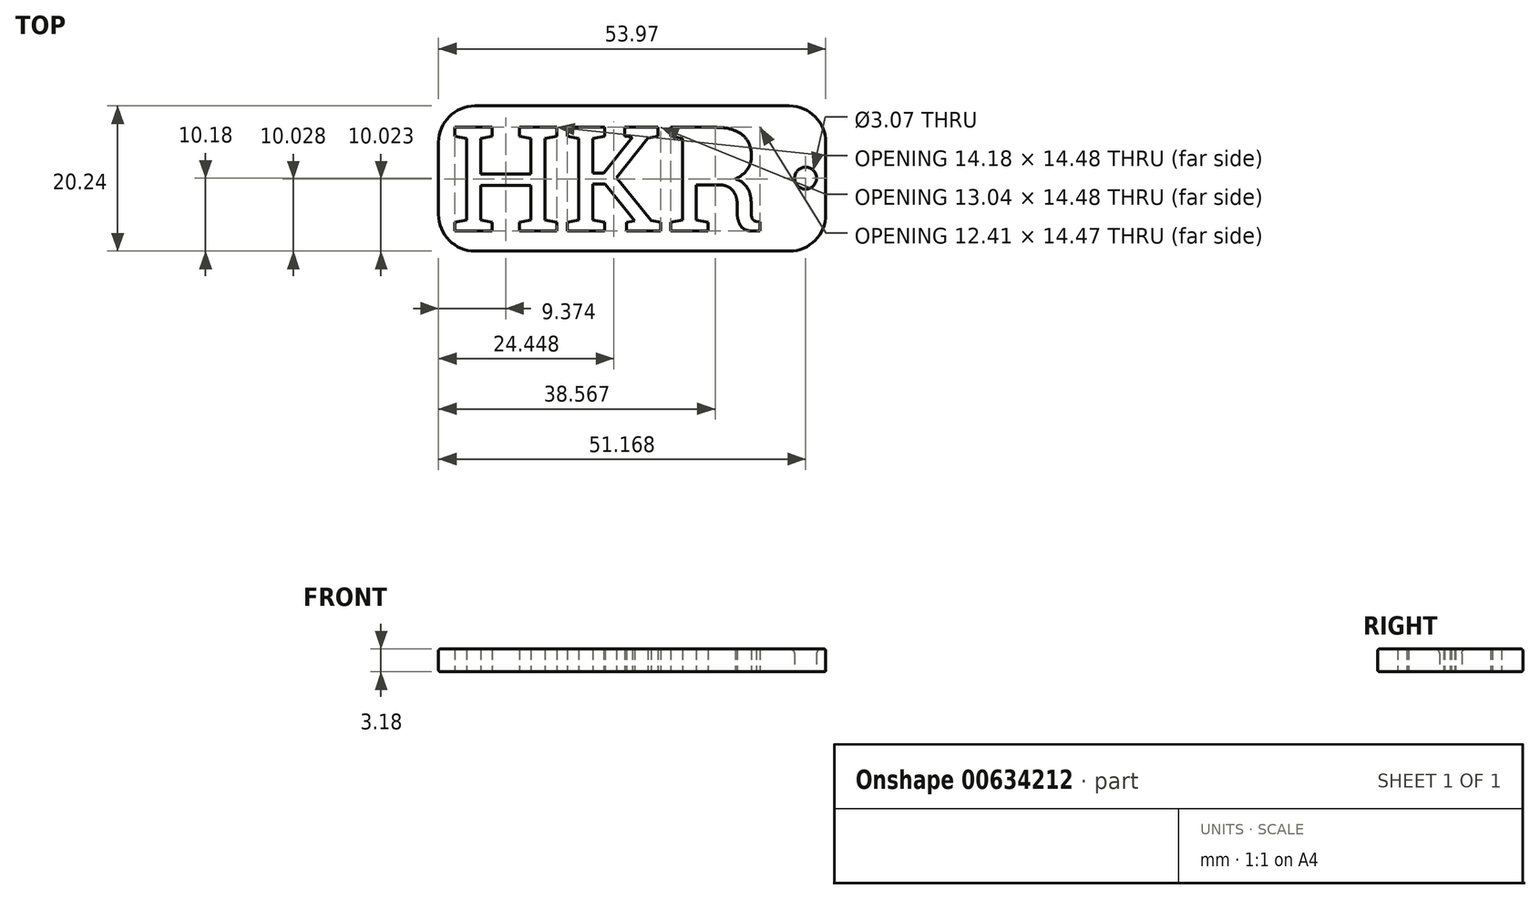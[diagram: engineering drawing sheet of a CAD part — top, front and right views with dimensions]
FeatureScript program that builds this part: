
annotation { "Feature Type Name" : "Feature", "Feature Type Description" : "" }
export const myFeature = defineFeature(function(context is Context, id is Id, definition is map)
    precondition{}
    {
        {
            var Q0;
            Q0=qCreatedBy(makeId("Top.planeOp"),FACE);
            var sketch = newSketch(context, id + "F0", { "sketchPlane" : qUnion([Q0])});
            skLineSegment(sketch, "E0.bottom", {"start": v(-77.06, 7.36) * mm, "end": v(-23.09, 7.36) * mm});
            skLineSegment(sketch, "E0.top", {"start": v(-77.06, -12.88) * mm, "end": v(-23.09, -12.88) * mm});
            skLineSegment(sketch, "E0.left", {"start": v(-77.06, 7.36) * mm, "end": v(-77.06, -12.88) * mm});
            skLineSegment(sketch, "E0.right", {"start": v(-23.09, 7.36) * mm, "end": v(-23.09, -12.88) * mm});
            skSolve(sketch);
        }
        {
            var Q0;
            Q0=makeQuery(id+"F0.imprint","IMPRINT",FACE,{"disambiguationData":[TD([[makeQuery(id+"F0.imprint","IMPRINT",EDGE,{"derivedFrom":sQuery(id+"F0.wireOp",EDGE,"E0.bottom")}),-1.0]])]});
            var sketch = newSketch(context, id + "F1", { "sketchPlane" : qUnion([Q0])});
            skText(sketch, "E1", { "text": "HKR", "fontName": "RobotoSlab-Regular.ttf"});
            const initialGuessF1  = {"E1": [-0.07548, -0.01009, 1, 0, 0.01466]};
            skSetInitialGuess(sketch, initialGuessF1);
            skSolve(sketch);
        }
        {
            var Q0;
            Q0=makeQuery(id+"F0.imprint","IMPRINT",FACE,{"disambiguationData":[TD([[makeQuery(id+"F0.imprint","IMPRINT",EDGE,{"derivedFrom":sQuery(id+"F0.wireOp",EDGE,"E0.bottom")}),-1.0]])]});
            var sketch = newSketch(context, id + "F2", { "sketchPlane" : qUnion([Q0])});
            skCircle(sketch, "E2", {"center": v(-25.9, -2.7) * mm, "radius": 1.53 * mm});
            skSolve(sketch);
        }
        {
            var Q0;
            Q0=makeQuery(id+"F0.imprint","IMPRINT",FACE,{"disambiguationData":[TD([[makeQuery(id+"F0.imprint","IMPRINT",EDGE,{"derivedFrom":sQuery(id+"F0.wireOp",EDGE,"E0.bottom")}),-1.0]])]});
            extrude(context, id + "F3", {"entities" : qUnion([Q0]), "depth" : 3.17 * mm, "offsetDistance" : 25.4 * mm});
        }
        {
            var Q0;
            Q0 = qSketchRegion(id + "F2", true);
            extrude(context, id + "F4", {"entities" : qUnion([Q0]), "operationType" : NewBodyOperationType.REMOVE, "depth" : 25.4 * mm, "offsetDistance" : 25.4 * mm});
        }
        {
            var Q0;
            Q0 = qSketchRegion(id + "F1", true);
            extrude(context, id + "F5", {"entities" : qUnion([Q0]), "operationType" : NewBodyOperationType.REMOVE, "depth" : 25.4 * mm, "offsetDistance" : 25.4 * mm});
        }
        {
            var Q0;
            Q0=makeQuery(id+"F3.opExtrude","SWEPT_EDGE",EDGE,{"disambiguationData":[OSD([sQuery(id+"F0.wireOp",EDGE,"E0.bottom"),sQuery(id+"F0.wireOp",EDGE,"E0.right")])]});
            fillet(context, id + "F6", {"entities" : qUnion([Q0]), "radius" : 5.08 * mm, "tangentPropagation" : true, "allowEdgeOverflow" : false});
        }
        {
            var Q0;
            Q0=makeQuery(id+"F3.opExtrude","SWEPT_EDGE",EDGE,{"disambiguationData":[OSD([sQuery(id+"F0.wireOp",EDGE,"E0.top"),sQuery(id+"F0.wireOp",EDGE,"E0.right")])]});
            fillet(context, id + "F7", {"entities" : qUnion([Q0]), "radius" : 5.08 * mm, "tangentPropagation" : true, "allowEdgeOverflow" : false});
        }
        {
            var Q0;
            Q0=makeQuery(id+"F3.opExtrude","SWEPT_EDGE",EDGE,{"disambiguationData":[OSD([sQuery(id+"F0.wireOp",EDGE,"E0.top"),sQuery(id+"F0.wireOp",EDGE,"E0.left")])]});
            fillet(context, id + "F8", {"entities" : qUnion([Q0]), "radius" : 5.08 * mm, "tangentPropagation" : true, "allowEdgeOverflow" : false});
        }
        {
            var Q0;
            Q0=makeQuery(id+"F3.opExtrude","SWEPT_EDGE",EDGE,{"disambiguationData":[OSD([sQuery(id+"F0.wireOp",EDGE,"E0.bottom"),sQuery(id+"F0.wireOp",EDGE,"E0.left")])]});
            fillet(context, id + "F9", {"entities" : qUnion([Q0]), "radius" : 5.08 * mm, "tangentPropagation" : true, "allowEdgeOverflow" : false});
        }
        {
            var Q0;
            Q0=makeQuery(id+"F4.boolean.opBoolean","INTERSECT",EDGE,{"derivedFrom":[makeQuery(id+"F3.opExtrude","CAP_FACE",FACE,{"disambiguationData":[OSD([sQuery(id+"F0.wireOp",EDGE,"E0.bottom"),sQuery(id+"F0.wireOp",EDGE,"E0.top"),sQuery(id+"F0.wireOp",EDGE,"E0.left"),sQuery(id+"F0.wireOp",EDGE,"E0.right")])],"isStart":false}),makeQuery(id+"F4.opExtrude","SWEPT_FACE",FACE,{"disambiguationData":[OSD([sQuery(id+"F2.wireOp",EDGE,"E2")])]})]});
            var Q1;
            Q1=makeQuery(id+"F4.boolean.opBoolean","COPY",EDGE,{"derivedFrom":makeQuery(id+"F4.opExtrude","CAP_EDGE",EDGE,{"disambiguationData":[OSD([sQuery(id+"F2.wireOp",EDGE,"E2")])],"isStart":true})});
            fillet(context, id + "F10", {"entities" : qUnion([Q0, Q1]), "radius" : 0.64 * mm, "tangentPropagation" : true, "allowEdgeOverflow" : false});
        }
        {
            var Q0;
            Q0=makeQuery(id+"F3.opExtrude","CAP_EDGE",EDGE,{"disambiguationData":[OSD([sQuery(id+"F0.wireOp",EDGE,"E0.bottom")])],"isStart":false});
            var Q1;
            {var subQ0=sQuery(id+"F0.wireOp",EDGE,"E0.left");var subQ1=sQuery(id+"F0.wireOp",EDGE,"E0.bottom");var subQ2=sQuery(id+"F0.wireOp",EDGE,"E0.right");var subQ3=sQuery(id+"F0.wireOp",EDGE,"E0.top");Q1=makeQuery(id+"F9.opFillet","BLEND_EDGE",EDGE,{"blendedFrom":[makeQuery(id+"F3.opExtrude","SWEPT_EDGE",EDGE,{"disambiguationData":[OSD([subQ1,subQ0])]}),makeQuery(id+"F5.boolean.opBoolean","SPLIT",FACE,{"disambiguationData":[TD([makeQuery(id+"F3.opExtrude","SWEPT_FACE",FACE,{"disambiguationData":[OSD([subQ1])]})])],"derivedFrom":makeQuery(id+"F3.opExtrude","CAP_FACE",FACE,{"disambiguationData":[OSD([subQ1,subQ3,subQ0,subQ2])],"isStart":false})})],"blendedInto":[makeQuery(id+"F5.boolean.opBoolean","SPLIT",FACE,{"disambiguationData":[TD([makeQuery(id+"F3.opExtrude","SWEPT_FACE",FACE,{"disambiguationData":[OSD([subQ1])]})])],"derivedFrom":makeQuery(id+"F3.opExtrude","CAP_FACE",FACE,{"disambiguationData":[OSD([subQ1,subQ3,subQ0,subQ2])],"isStart":false})})]});}
            var Q2;
            Q2=makeQuery(id+"F3.opExtrude","CAP_EDGE",EDGE,{"disambiguationData":[OSD([sQuery(id+"F0.wireOp",EDGE,"E0.left")])],"isStart":false});
            var Q3;
            {var subQ0=sQuery(id+"F0.wireOp",EDGE,"E0.left");var subQ1=sQuery(id+"F0.wireOp",EDGE,"E0.bottom");var subQ2=sQuery(id+"F0.wireOp",EDGE,"E0.right");var subQ3=sQuery(id+"F0.wireOp",EDGE,"E0.top");Q3=makeQuery(id+"F8.opFillet","BLEND_EDGE",EDGE,{"blendedFrom":[makeQuery(id+"F3.opExtrude","SWEPT_EDGE",EDGE,{"disambiguationData":[OSD([subQ3,subQ0])]}),makeQuery(id+"F5.boolean.opBoolean","SPLIT",FACE,{"disambiguationData":[TD([makeQuery(id+"F3.opExtrude","SWEPT_FACE",FACE,{"disambiguationData":[OSD([subQ1])]})])],"derivedFrom":makeQuery(id+"F3.opExtrude","CAP_FACE",FACE,{"disambiguationData":[OSD([subQ1,subQ3,subQ0,subQ2])],"isStart":false})})],"blendedInto":[makeQuery(id+"F5.boolean.opBoolean","SPLIT",FACE,{"disambiguationData":[TD([makeQuery(id+"F3.opExtrude","SWEPT_FACE",FACE,{"disambiguationData":[OSD([subQ1])]})])],"derivedFrom":makeQuery(id+"F3.opExtrude","CAP_FACE",FACE,{"disambiguationData":[OSD([subQ1,subQ3,subQ0,subQ2])],"isStart":false})})]});}
            var Q4;
            Q4=makeQuery(id+"F3.opExtrude","CAP_EDGE",EDGE,{"disambiguationData":[OSD([sQuery(id+"F0.wireOp",EDGE,"E0.top")])],"isStart":false});
            var Q5;
            {var subQ0=sQuery(id+"F0.wireOp",EDGE,"E0.left");var subQ1=sQuery(id+"F0.wireOp",EDGE,"E0.bottom");var subQ2=sQuery(id+"F0.wireOp",EDGE,"E0.right");var subQ3=sQuery(id+"F0.wireOp",EDGE,"E0.top");Q5=makeQuery(id+"F6.opFillet","BLEND_EDGE",EDGE,{"blendedFrom":[makeQuery(id+"F3.opExtrude","SWEPT_EDGE",EDGE,{"disambiguationData":[OSD([subQ1,subQ2])]}),makeQuery(id+"F5.boolean.opBoolean","SPLIT",FACE,{"disambiguationData":[TD([makeQuery(id+"F3.opExtrude","SWEPT_FACE",FACE,{"disambiguationData":[OSD([subQ1])]})])],"derivedFrom":makeQuery(id+"F3.opExtrude","CAP_FACE",FACE,{"disambiguationData":[OSD([subQ1,subQ3,subQ0,subQ2])],"isStart":false})})],"blendedInto":[makeQuery(id+"F5.boolean.opBoolean","SPLIT",FACE,{"disambiguationData":[TD([makeQuery(id+"F3.opExtrude","SWEPT_FACE",FACE,{"disambiguationData":[OSD([subQ1])]})])],"derivedFrom":makeQuery(id+"F3.opExtrude","CAP_FACE",FACE,{"disambiguationData":[OSD([subQ1,subQ3,subQ0,subQ2])],"isStart":false})})]});}
            var Q6;
            Q6=makeQuery(id+"F3.opExtrude","CAP_EDGE",EDGE,{"disambiguationData":[OSD([sQuery(id+"F0.wireOp",EDGE,"E0.right")])],"isStart":true});
            var Q7;
            {var subQ0=sQuery(id+"F0.wireOp",EDGE,"E0.left");var subQ1=sQuery(id+"F0.wireOp",EDGE,"E0.bottom");var subQ2=sQuery(id+"F0.wireOp",EDGE,"E0.right");var subQ3=sQuery(id+"F0.wireOp",EDGE,"E0.top");Q7=makeQuery(id+"F7.opFillet","BLEND_EDGE",EDGE,{"blendedFrom":[makeQuery(id+"F3.opExtrude","SWEPT_EDGE",EDGE,{"disambiguationData":[OSD([subQ3,subQ2])]}),makeQuery(id+"F5.boolean.opBoolean","SPLIT",FACE,{"disambiguationData":[TD([makeQuery(id+"F3.opExtrude","SWEPT_FACE",FACE,{"disambiguationData":[OSD([subQ1])]})])],"derivedFrom":makeQuery(id+"F3.opExtrude","CAP_FACE",FACE,{"disambiguationData":[OSD([subQ1,subQ3,subQ0,subQ2])],"isStart":false})})],"blendedInto":[makeQuery(id+"F5.boolean.opBoolean","SPLIT",FACE,{"disambiguationData":[TD([makeQuery(id+"F3.opExtrude","SWEPT_FACE",FACE,{"disambiguationData":[OSD([subQ1])]})])],"derivedFrom":makeQuery(id+"F3.opExtrude","CAP_FACE",FACE,{"disambiguationData":[OSD([subQ1,subQ3,subQ0,subQ2])],"isStart":false})})]});}
            var Q8;
            Q8=makeQuery(id+"F3.opExtrude","CAP_EDGE",EDGE,{"disambiguationData":[OSD([sQuery(id+"F0.wireOp",EDGE,"E0.right")])],"isStart":false});
            var Q9;
            {var subQ0=sQuery(id+"F0.wireOp",EDGE,"E0.left");var subQ1=sQuery(id+"F0.wireOp",EDGE,"E0.bottom");var subQ2=sQuery(id+"F0.wireOp",EDGE,"E0.right");var subQ3=sQuery(id+"F0.wireOp",EDGE,"E0.top");Q9=makeQuery(id+"F6.opFillet","BLEND_EDGE",EDGE,{"blendedFrom":[makeQuery(id+"F3.opExtrude","SWEPT_EDGE",EDGE,{"disambiguationData":[OSD([subQ1,subQ2])]}),makeQuery(id+"F5.boolean.opBoolean","SPLIT",FACE,{"disambiguationData":[TD([makeQuery(id+"F3.opExtrude","SWEPT_FACE",FACE,{"disambiguationData":[OSD([subQ1])]})])],"derivedFrom":makeQuery(id+"F3.opExtrude","CAP_FACE",FACE,{"disambiguationData":[OSD([subQ1,subQ3,subQ0,subQ2])],"isStart":true})})],"blendedInto":[makeQuery(id+"F5.boolean.opBoolean","SPLIT",FACE,{"disambiguationData":[TD([makeQuery(id+"F3.opExtrude","SWEPT_FACE",FACE,{"disambiguationData":[OSD([subQ1])]})])],"derivedFrom":makeQuery(id+"F3.opExtrude","CAP_FACE",FACE,{"disambiguationData":[OSD([subQ1,subQ3,subQ0,subQ2])],"isStart":true})})]});}
            var Q10;
            Q10=makeQuery(id+"F3.opExtrude","CAP_EDGE",EDGE,{"disambiguationData":[OSD([sQuery(id+"F0.wireOp",EDGE,"E0.bottom")])],"isStart":true});
            var Q11;
            {var subQ0=sQuery(id+"F0.wireOp",EDGE,"E0.left");var subQ1=sQuery(id+"F0.wireOp",EDGE,"E0.bottom");var subQ2=sQuery(id+"F0.wireOp",EDGE,"E0.right");var subQ3=sQuery(id+"F0.wireOp",EDGE,"E0.top");Q11=makeQuery(id+"F7.opFillet","BLEND_EDGE",EDGE,{"blendedFrom":[makeQuery(id+"F3.opExtrude","SWEPT_EDGE",EDGE,{"disambiguationData":[OSD([subQ3,subQ2])]}),makeQuery(id+"F5.boolean.opBoolean","SPLIT",FACE,{"disambiguationData":[TD([makeQuery(id+"F3.opExtrude","SWEPT_FACE",FACE,{"disambiguationData":[OSD([subQ1])]})])],"derivedFrom":makeQuery(id+"F3.opExtrude","CAP_FACE",FACE,{"disambiguationData":[OSD([subQ1,subQ3,subQ0,subQ2])],"isStart":true})})],"blendedInto":[makeQuery(id+"F5.boolean.opBoolean","SPLIT",FACE,{"disambiguationData":[TD([makeQuery(id+"F3.opExtrude","SWEPT_FACE",FACE,{"disambiguationData":[OSD([subQ1])]})])],"derivedFrom":makeQuery(id+"F3.opExtrude","CAP_FACE",FACE,{"disambiguationData":[OSD([subQ1,subQ3,subQ0,subQ2])],"isStart":true})})]});}
            var Q12;
            {var subQ0=sQuery(id+"F0.wireOp",EDGE,"E0.left");var subQ1=sQuery(id+"F0.wireOp",EDGE,"E0.bottom");var subQ2=sQuery(id+"F0.wireOp",EDGE,"E0.right");var subQ3=sQuery(id+"F0.wireOp",EDGE,"E0.top");Q12=makeQuery(id+"F9.opFillet","BLEND_EDGE",EDGE,{"blendedFrom":[makeQuery(id+"F3.opExtrude","SWEPT_EDGE",EDGE,{"disambiguationData":[OSD([subQ1,subQ0])]}),makeQuery(id+"F5.boolean.opBoolean","SPLIT",FACE,{"disambiguationData":[TD([makeQuery(id+"F3.opExtrude","SWEPT_FACE",FACE,{"disambiguationData":[OSD([subQ1])]})])],"derivedFrom":makeQuery(id+"F3.opExtrude","CAP_FACE",FACE,{"disambiguationData":[OSD([subQ1,subQ3,subQ0,subQ2])],"isStart":true})})],"blendedInto":[makeQuery(id+"F5.boolean.opBoolean","SPLIT",FACE,{"disambiguationData":[TD([makeQuery(id+"F3.opExtrude","SWEPT_FACE",FACE,{"disambiguationData":[OSD([subQ1])]})])],"derivedFrom":makeQuery(id+"F3.opExtrude","CAP_FACE",FACE,{"disambiguationData":[OSD([subQ1,subQ3,subQ0,subQ2])],"isStart":true})})]});}
            var Q13;
            Q13=makeQuery(id+"F3.opExtrude","CAP_EDGE",EDGE,{"disambiguationData":[OSD([sQuery(id+"F0.wireOp",EDGE,"E0.left")])],"isStart":true});
            var Q14;
            {var subQ0=sQuery(id+"F0.wireOp",EDGE,"E0.left");var subQ1=sQuery(id+"F0.wireOp",EDGE,"E0.bottom");var subQ2=sQuery(id+"F0.wireOp",EDGE,"E0.right");var subQ3=sQuery(id+"F0.wireOp",EDGE,"E0.top");Q14=makeQuery(id+"F8.opFillet","BLEND_EDGE",EDGE,{"blendedFrom":[makeQuery(id+"F3.opExtrude","SWEPT_EDGE",EDGE,{"disambiguationData":[OSD([subQ3,subQ0])]}),makeQuery(id+"F5.boolean.opBoolean","SPLIT",FACE,{"disambiguationData":[TD([makeQuery(id+"F3.opExtrude","SWEPT_FACE",FACE,{"disambiguationData":[OSD([subQ1])]})])],"derivedFrom":makeQuery(id+"F3.opExtrude","CAP_FACE",FACE,{"disambiguationData":[OSD([subQ1,subQ3,subQ0,subQ2])],"isStart":true})})],"blendedInto":[makeQuery(id+"F5.boolean.opBoolean","SPLIT",FACE,{"disambiguationData":[TD([makeQuery(id+"F3.opExtrude","SWEPT_FACE",FACE,{"disambiguationData":[OSD([subQ1])]})])],"derivedFrom":makeQuery(id+"F3.opExtrude","CAP_FACE",FACE,{"disambiguationData":[OSD([subQ1,subQ3,subQ0,subQ2])],"isStart":true})})]});}
            var Q15;
            Q15=makeQuery(id+"F3.opExtrude","CAP_EDGE",EDGE,{"disambiguationData":[OSD([sQuery(id+"F0.wireOp",EDGE,"E0.top")])],"isStart":true});
            fillet(context, id + "F11", {"entities" : qUnion([Q0, Q1, Q2, Q3, Q4, Q5, Q6, Q7, Q8, Q9, Q10, Q11, Q12, Q13, Q14, Q15]), "radius" : 0.25 * mm, "tangentPropagation" : true, "allowEdgeOverflow" : false});
        }
        {
            var Q0;
            Q0=makeQuery(id+"F5.boolean.opBoolean","SPLIT",FACE,{"disambiguationData":[TD([makeQuery(id+"F5.opExtrude","SWEPT_FACE",FACE,{"disambiguationData":[OSD([sQuery(id+"F1.wireOp",EDGE,"E1.sketch_text.stroke-88")])]})])],"derivedFrom":makeQuery(id+"F3.opExtrude","CAP_FACE",FACE,{"disambiguationData":[OSD([sQuery(id+"F0.wireOp",EDGE,"E0.bottom"),sQuery(id+"F0.wireOp",EDGE,"E0.top"),sQuery(id+"F0.wireOp",EDGE,"E0.left"),sQuery(id+"F0.wireOp",EDGE,"E0.right")])],"isStart":false})});
            extrude(context, id + "F12", {"entities" : qUnion([Q0]), "operationType" : NewBodyOperationType.REMOVE, "oppositeDirection" : true, "depth" : 25.4 * mm, "offsetDistance" : 25.4 * mm});
        }
    });
